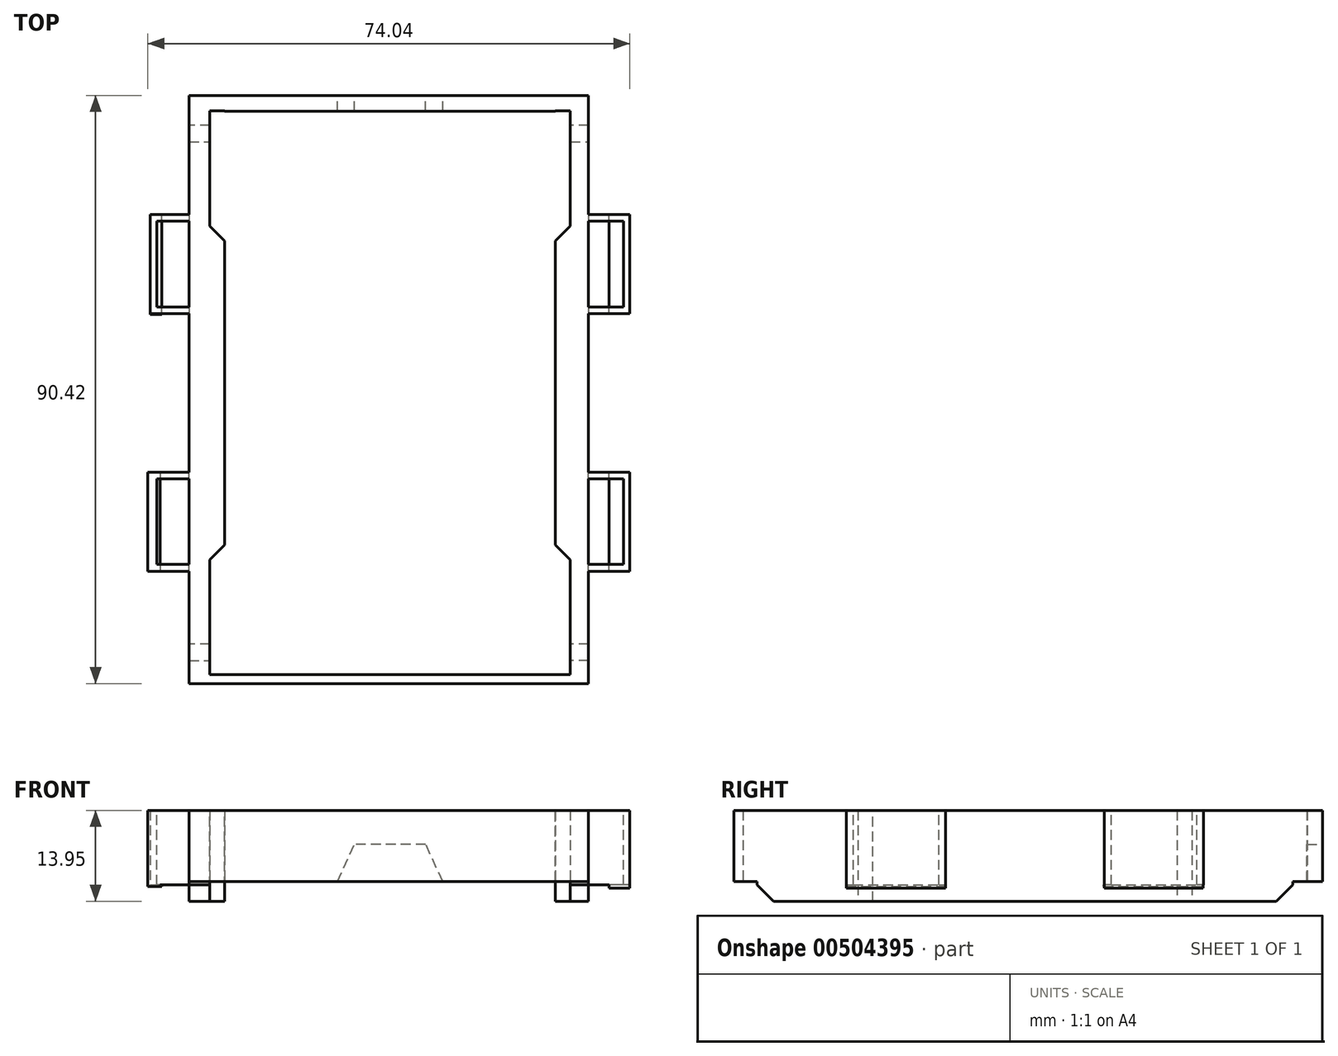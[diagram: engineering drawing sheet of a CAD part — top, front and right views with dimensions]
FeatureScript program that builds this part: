
annotation { "Feature Type Name" : "Feature", "Feature Type Description" : "" }
export const myFeature = defineFeature(function(context is Context, id is Id, definition is map)
    precondition{}
    {
        {
            var Q0;
            Q0=qCreatedBy(makeId("Top.planeOp"),FACE);
            var sketch = newSketch(context, id + "F0", { "sketchPlane" : qUnion([Q0])});
            skLineSegment(sketch, "E0.bottom", {"start": v(-30.48, 45.72) * mm, "end": v(30.48, 45.72) * mm});
            skLineSegment(sketch, "E0.top", {"start": v(-30.48, -45.72) * mm, "end": v(30.48, -45.72) * mm});
            skLineSegment(sketch, "E0.left", {"start": v(-30.48, 45.72) * mm, "end": v(-30.48, -45.72) * mm});
            skLineSegment(sketch, "E0.right", {"start": v(30.48, 45.72) * mm, "end": v(30.48, -45.72) * mm});
            skPoint(sketch, "E0.middle", {"position": v(0, 0) * mm});
            skLineSegment(sketch, "E1.bottom", {"start": v(-25.4, 43.3) * mm, "end": v(25.4, 43.3) * mm});
            skLineSegment(sketch, "E1.top", {"start": v(-25.4, -43.3) * mm, "end": v(25.4, -43.3) * mm});
            skLineSegment(sketch, "E1.left", {"start": v(-25.4, 43.3) * mm, "end": v(-25.4, -43.3) * mm});
            skLineSegment(sketch, "E1.right", {"start": v(25.4, 43.3) * mm, "end": v(25.4, -43.3) * mm});
            skSolve(sketch);
        }
        {
            var Q0;
            Q0=makeQuery(id+"F0.imprint","IMPRINT",FACE,{"disambiguationData":[TD([[makeQuery(id+"F0.imprint","IMPRINT",EDGE,{"derivedFrom":sQuery(id+"F0.wireOp",EDGE,"E0.bottom")}),-1.0]])]});
            extrude(context, id + "F1", {"entities" : qUnion([Q0]), "depth" : 28.45 * mm});
        }
        {
            var Q0;
            Q0=makeQuery(id+"F1.opExtrude","SWEPT_FACE",FACE,{"disambiguationData":[OSD([sQuery(id+"F0.wireOp",EDGE,"E0.bottom")])]});
            var sketch = newSketch(context, id + "F2", { "sketchPlane" : qUnion([Q0])});
            skLineSegment(sketch, "E2", {"start": v(30.48, 14.22) * mm, "end": v(-30.48, 14.22) * mm, "construction": true});
            skPoint(sketch, "E3.middle", {"position": v(0, 28.45) * mm});
            skLineSegment(sketch, "E4", {"start": v(0, 0) * mm, "end": v(-9.48, 0) * mm});
            skLineSegment(sketch, "E5.bottom", {"start": v(-5.46, 19.69) * mm, "end": v(5.46, 19.69) * mm});
            skLineSegment(sketch, "E5.top", {"start": v(-5.46, 8.76) * mm, "end": v(5.46, 8.76) * mm});
            skPoint(sketch, "E5.middle", {"position": v(0, 14.22) * mm});
            skLineSegment(sketch, "E6", {"start": v(-9.48, 0) * mm, "end": v(-5.46, 8.76) * mm});
            skLineSegment(sketch, "E7.MirrorCS", {"start": v(0, 0) * mm, "end": v(9.48, 0) * mm});
            skLineSegment(sketch, "E8.MirrorCS", {"start": v(9.48, 0) * mm, "end": v(5.46, 8.76) * mm});
            skLineSegment(sketch, "E9.MirrorCS", {"start": v(-5.46, 19.68) * mm, "end": v(5.46, 19.68) * mm});
            skLineSegment(sketch, "E10.MirrorCS", {"start": v(-9.48, 28.45) * mm, "end": v(-5.46, 19.68) * mm});
            skLineSegment(sketch, "E11.MirrorCS", {"start": v(0, 28.45) * mm, "end": v(-9.48, 28.45) * mm});
            skLineSegment(sketch, "E12.MirrorCS", {"start": v(0, 28.45) * mm, "end": v(9.48, 28.45) * mm});
            skLineSegment(sketch, "E13.MirrorCS", {"start": v(9.48, 28.45) * mm, "end": v(5.46, 19.68) * mm});
            skSolve(sketch);
        }
        {
            var Q0;
            Q0=qSketchRegion(id+"F2",true);
            var Q1;
            {var subQ1=sQuery(id+"F2.wireOp",EDGE,"z2dX2tQm-mAHQ-A0xj-hADe-n06FKAJlfdiZ.bottom");Q1=makeQuery(id+"F2.imprint","IMPRINT",FACE,{"disambiguationData":[TD([[makeQuery(id+"F2.imprint","IMPRINT",EDGE,{"derivedFrom":subQ1}),-1.0]])]});}
            extrude(context, id + "F3", {"entities" : qUnion([Q0, Q1]), "operationType" : NewBodyOperationType.REMOVE, "oppositeDirection" : true, "depth" : 25.4 * mm});
        }
        {
            var Q0;
            Q0=qCreatedBy(makeId("Top.planeOp"),FACE);
            var sketch = newSketch(context, id + "F4", { "sketchPlane" : qUnion([Q0])});
            skLineSegment(sketch, "E14.bottom", {"start": v(33.22, 48.14) * mm, "end": v(-33.43, 48.14) * mm});
            skLineSegment(sketch, "E14.top", {"start": v(33.22, 41.15) * mm, "end": v(-33.43, 41.15) * mm});
            skLineSegment(sketch, "E14.left", {"start": v(33.22, 48.14) * mm, "end": v(33.22, 41.15) * mm});
            skLineSegment(sketch, "E14.right", {"start": v(-33.43, 48.14) * mm, "end": v(-33.43, 41.15) * mm});
            skLineSegment(sketch, "E15.MirrorCS", {"start": v(33.22, -41.15) * mm, "end": v(-33.43, -41.15) * mm});
            skLineSegment(sketch, "E16.MirrorCS", {"start": v(33.22, -48.14) * mm, "end": v(33.22, -41.15) * mm});
            skLineSegment(sketch, "E17.MirrorCS", {"start": v(-33.43, -48.14) * mm, "end": v(-33.43, -41.15) * mm});
            skLineSegment(sketch, "E18.MirrorCS", {"start": v(33.22, -48.14) * mm, "end": v(-33.43, -48.14) * mm});
            skSolve(sketch);
        }
        {
            var Q0;
            Q0=qSketchRegion(id+"F4",true);
            extrude(context, id + "F5", {"entities" : qUnion([Q0]), "operationType" : NewBodyOperationType.REMOVE, "depth" : 3.05 * mm});
        }
        {
            var Q0;
            Q0=makeQuery(id+"F1.opExtrude","CAP_FACE",FACE,{"disambiguationData":[OSD([sQuery(id+"F0.wireOp",EDGE,"E0.bottom"),sQuery(id+"F0.wireOp",EDGE,"E0.top"),sQuery(id+"F0.wireOp",EDGE,"E0.left"),sQuery(id+"F0.wireOp",EDGE,"E0.right"),sQuery(id+"F0.wireOp",EDGE,"E1.bottom"),sQuery(id+"F0.wireOp",EDGE,"E1.top"),sQuery(id+"F0.wireOp",EDGE,"E1.left"),sQuery(id+"F0.wireOp",EDGE,"E1.right")])],"isStart":false});
            var sketch = newSketch(context, id + "F6", { "sketchPlane" : qUnion([Q0])});
            skLineSegment(sketch, "E19.bottom", {"start": v(30.48, 45.72) * mm, "end": v(-34.49, 45.72) * mm});
            skLineSegment(sketch, "E19.top", {"start": v(30.48, 40.94) * mm, "end": v(-34.49, 40.94) * mm});
            skLineSegment(sketch, "E19.left", {"start": v(30.48, 45.72) * mm, "end": v(30.48, 40.94) * mm});
            skLineSegment(sketch, "E19.right", {"start": v(-34.49, 45.72) * mm, "end": v(-34.49, 40.94) * mm});
            skLineSegment(sketch, "E20.MirrorCS", {"start": v(30.48, -40.94) * mm, "end": v(-34.49, -40.94) * mm});
            skLineSegment(sketch, "E21.MirrorCS", {"start": v(30.48, -45.72) * mm, "end": v(30.48, -40.94) * mm});
            skLineSegment(sketch, "E22.MirrorCS", {"start": v(-34.49, -45.72) * mm, "end": v(-34.49, -40.94) * mm});
            skLineSegment(sketch, "E23.MirrorCS", {"start": v(30.48, -45.72) * mm, "end": v(-34.49, -45.72) * mm});
            skSolve(sketch);
        }
        {
            var Q0;
            Q0=qSketchRegion(id+"F6",true);
            extrude(context, id + "F7", {"entities" : qUnion([Q0]), "operationType" : NewBodyOperationType.REMOVE, "oppositeDirection" : true, "depth" : 3.05 * mm});
        }
        {
            var Q0;
            Q0=makeQuery(id+"F1.opExtrude","SWEPT_FACE",FACE,{"disambiguationData":[OSD([sQuery(id+"F0.wireOp",EDGE,"E1.right")])]});
            var sketch = newSketch(context, id + "F8", { "sketchPlane" : qUnion([Q0])});
            skLineSegment(sketch, "E24.bottom", {"start": v(-41.15, 0) * mm, "end": v(-25.91, 0) * mm});
            skLineSegment(sketch, "E24.top", {"start": v(-41.15, 30.48) * mm, "end": v(-25.91, 30.48) * mm});
            skLineSegment(sketch, "E24.right", {"start": v(-25.91, 0) * mm, "end": v(-25.91, 30.48) * mm});
            skLineSegment(sketch, "E25", {"start": v(0, 0) * mm, "end": v(0, 28.45) * mm, "construction": true});
            skLineSegment(sketch, "E26.MirrorCS", {"start": v(25.91, 0) * mm, "end": v(25.91, 30.48) * mm});
            skLineSegment(sketch, "E27.MirrorCS", {"start": v(41.15, 30.48) * mm, "end": v(25.91, 30.48) * mm});
            skLineSegment(sketch, "E28.MirrorCS", {"start": v(41.15, 0) * mm, "end": v(25.91, 0) * mm});
            skLineSegment(sketch, "E29", {"start": v(-41.15, 30.48) * mm, "end": v(-43.09, 30.48) * mm});
            skLineSegment(sketch, "E30", {"start": v(-43.09, 30.48) * mm, "end": v(-43.09, 0) * mm});
            skLineSegment(sketch, "E31", {"start": v(-43.09, 0) * mm, "end": v(-41.15, 0) * mm});
            skLineSegment(sketch, "E32.MirrorCS", {"start": v(41.15, 30.48) * mm, "end": v(43.09, 30.48) * mm});
            skLineSegment(sketch, "E33.MirrorCS", {"start": v(43.09, 30.48) * mm, "end": v(43.09, 0) * mm});
            skLineSegment(sketch, "E34.MirrorCS", {"start": v(43.09, 0) * mm, "end": v(41.15, 0) * mm});
            skSolve(sketch);
        }
        {
            var Q0;
            Q0=qSketchRegion(id+"F8",true);
            extrude(context, id + "F9", {"entities" : qUnion([Q0]), "operationType" : NewBodyOperationType.REMOVE, "oppositeDirection" : true, "depth" : 2.3 * mm});
        }
        {
            var Q0;
            Q0=qCreatedBy(makeId("Right.planeOp"),FACE);
            var sketch = newSketch(context, id + "F10", { "sketchPlane" : qUnion([Q0])});
            skLineSegment(sketch, "E35.bottom", {"start": v(51.68, -10.67) * mm, "end": v(-48.17, -10.67) * mm});
            skLineSegment(sketch, "E35.top", {"start": v(51.68, 37.54) * mm, "end": v(-48.17, 37.54) * mm});
            skLineSegment(sketch, "E35.left", {"start": v(51.68, -10.67) * mm, "end": v(51.68, 37.54) * mm});
            skLineSegment(sketch, "E35.right", {"start": v(-48.17, -10.67) * mm, "end": v(-48.17, 37.54) * mm});
            skSolve(sketch);
        }
        {
            var Q0;
            Q0=qSketchRegion(id+"F10",true);
            extrude(context, id + "F11", {"entities" : qUnion([Q0]), "operationType" : NewBodyOperationType.REMOVE, "oppositeDirection" : true, "depth" : 50.8 * mm});
        }
        {
            var Q0;
            Q0=makeQuery(id+"F1.opExtrude","SWEPT_BODY",BODY,{"disambiguationData":[OSD([sQuery(id+"F0.wireOp",EDGE,"E0.bottom"),sQuery(id+"F0.wireOp",EDGE,"E0.top"),sQuery(id+"F0.wireOp",EDGE,"E0.left"),sQuery(id+"F0.wireOp",EDGE,"E0.right"),sQuery(id+"F0.wireOp",EDGE,"E1.bottom"),sQuery(id+"F0.wireOp",EDGE,"E1.top"),sQuery(id+"F0.wireOp",EDGE,"E1.left"),sQuery(id+"F0.wireOp",EDGE,"E1.right")])]});
            var Q1;
            Q1=qCreatedBy(makeId("Right.planeOp"),FACE);
            mirror(context, id + "F12", {"operationType" : NewBodyOperationType.ADD, "entities" : qUnion([Q0]), "mirrorPlane" : qUnion([Q1])});
        }
        {
            var Q0;
            {var subQ1=sQuery(id+"F0.wireOp",EDGE,"E0.right");var subQ2=sQuery(id+"F6.wireOp",EDGE,"E19.top");Q0=makeQuery(id+"F12.opPattern","COPY",EDGE,{"derivedFrom":makeQuery(id+"F7.boolean.opBoolean","COPY",EDGE,{"disambiguationData":[TD([makeQuery(id+"F1.opExtrude","SWEPT_FACE",FACE,{"disambiguationData":[OSD([subQ1])]})])],"derivedFrom":makeQuery(id+"F7.opExtrude","CAP_EDGE",EDGE,{"disambiguationData":[OSD([subQ2])],"isStart":true})}),"instanceName":"1"});}
            var Q1;
            {var subQ1=sQuery(id+"F0.wireOp",EDGE,"E0.right");var subQ2=sQuery(id+"F4.wireOp",EDGE,"E14.top");Q1=makeQuery(id+"F12.opPattern","COPY",EDGE,{"derivedFrom":makeQuery(id+"F5.boolean.opBoolean","COPY",EDGE,{"disambiguationData":[TD([makeQuery(id+"F1.opExtrude","SWEPT_FACE",FACE,{"disambiguationData":[OSD([subQ1])]})])],"derivedFrom":makeQuery(id+"F5.opExtrude","CAP_EDGE",EDGE,{"disambiguationData":[OSD([subQ2])],"isStart":true})}),"instanceName":"1"});}
            var Q2;
            {var subQ1=sQuery(id+"F0.wireOp",EDGE,"E0.right");var subQ2=sQuery(id+"F6.wireOp",EDGE,"E19.top");Q2=makeQuery(id+"F7.boolean.opBoolean","COPY",EDGE,{"disambiguationData":[TD([makeQuery(id+"F1.opExtrude","SWEPT_FACE",FACE,{"disambiguationData":[OSD([subQ1])]})])],"derivedFrom":makeQuery(id+"F7.opExtrude","CAP_EDGE",EDGE,{"disambiguationData":[OSD([subQ2])],"isStart":true})});}
            var Q3;
            {var subQ1=sQuery(id+"F0.wireOp",EDGE,"E0.right");var subQ2=sQuery(id+"F6.wireOp",EDGE,"E20.MirrorCS");Q3=makeQuery(id+"F7.boolean.opBoolean","COPY",EDGE,{"disambiguationData":[TD([makeQuery(id+"F1.opExtrude","SWEPT_FACE",FACE,{"disambiguationData":[OSD([subQ1])]})])],"derivedFrom":makeQuery(id+"F7.opExtrude","CAP_EDGE",EDGE,{"disambiguationData":[OSD([subQ2])],"isStart":true})});}
            var Q4;
            {var subQ1=sQuery(id+"F0.wireOp",EDGE,"E0.right");var subQ2=sQuery(id+"F6.wireOp",EDGE,"E20.MirrorCS");Q4=makeQuery(id+"F12.opPattern","COPY",EDGE,{"derivedFrom":makeQuery(id+"F7.boolean.opBoolean","COPY",EDGE,{"disambiguationData":[TD([makeQuery(id+"F1.opExtrude","SWEPT_FACE",FACE,{"disambiguationData":[OSD([subQ1])]})])],"derivedFrom":makeQuery(id+"F7.opExtrude","CAP_EDGE",EDGE,{"disambiguationData":[OSD([subQ2])],"isStart":true})}),"instanceName":"1"});}
            var Q5;
            {var subQ1=sQuery(id+"F0.wireOp",EDGE,"E0.right");var subQ2=sQuery(id+"F4.wireOp",EDGE,"E15.MirrorCS");Q5=makeQuery(id+"F12.opPattern","COPY",EDGE,{"derivedFrom":makeQuery(id+"F5.boolean.opBoolean","COPY",EDGE,{"disambiguationData":[TD([makeQuery(id+"F1.opExtrude","SWEPT_FACE",FACE,{"disambiguationData":[OSD([subQ1])]})])],"derivedFrom":makeQuery(id+"F5.opExtrude","CAP_EDGE",EDGE,{"disambiguationData":[OSD([subQ2])],"isStart":true})}),"instanceName":"1"});}
            var Q6;
            {var subQ1=sQuery(id+"F0.wireOp",EDGE,"E0.right");var subQ2=sQuery(id+"F4.wireOp",EDGE,"E15.MirrorCS");Q6=makeQuery(id+"F5.boolean.opBoolean","COPY",EDGE,{"disambiguationData":[TD([makeQuery(id+"F1.opExtrude","SWEPT_FACE",FACE,{"disambiguationData":[OSD([subQ1])]})])],"derivedFrom":makeQuery(id+"F5.opExtrude","CAP_EDGE",EDGE,{"disambiguationData":[OSD([subQ2])],"isStart":true})});}
            var Q7;
            {var subQ1=sQuery(id+"F0.wireOp",EDGE,"E0.right");var subQ2=sQuery(id+"F4.wireOp",EDGE,"E14.top");Q7=makeQuery(id+"F5.boolean.opBoolean","COPY",EDGE,{"disambiguationData":[TD([makeQuery(id+"F1.opExtrude","SWEPT_FACE",FACE,{"disambiguationData":[OSD([subQ1])]})])],"derivedFrom":makeQuery(id+"F5.opExtrude","CAP_EDGE",EDGE,{"disambiguationData":[OSD([subQ2])],"isStart":true})});}
            var Q8;
            Q8=makeQuery(id+"F9.boolean.opBoolean","COPY",EDGE,{"derivedFrom":makeQuery(id+"F9.opExtrude","CAP_EDGE",EDGE,{"disambiguationData":[OSD([sQuery(id+"F8.wireOp",EDGE,"E24.right")])],"isStart":true})});
            var Q9;
            Q9=makeQuery(id+"F9.boolean.opBoolean","COPY",EDGE,{"derivedFrom":makeQuery(id+"F9.opExtrude","CAP_EDGE",EDGE,{"disambiguationData":[OSD([sQuery(id+"F8.wireOp",EDGE,"E26.MirrorCS")])],"isStart":true})});
            var Q10;
            Q10=makeQuery(id+"F12.opPattern","COPY",EDGE,{"derivedFrom":makeQuery(id+"F9.boolean.opBoolean","COPY",EDGE,{"derivedFrom":makeQuery(id+"F9.opExtrude","CAP_EDGE",EDGE,{"disambiguationData":[OSD([sQuery(id+"F8.wireOp",EDGE,"E24.right")])],"isStart":true})}),"instanceName":"1"});
            var Q11;
            Q11=makeQuery(id+"F12.opPattern","COPY",EDGE,{"derivedFrom":makeQuery(id+"F9.boolean.opBoolean","COPY",EDGE,{"derivedFrom":makeQuery(id+"F9.opExtrude","CAP_EDGE",EDGE,{"disambiguationData":[OSD([sQuery(id+"F8.wireOp",EDGE,"E26.MirrorCS")])],"isStart":true})}),"instanceName":"1"});
            chamfer(context, id + "F13", {"entities" : qUnion([Q0, Q1, Q2, Q3, Q4, Q5, Q6, Q7, Q8, Q9, Q10, Q11]), "width" : 2.54 * mm, "tangentPropagation" : true});
        }
        {
            var Q0;
            Q0=makeQuery(id+"F1.opExtrude","SWEPT_FACE",FACE,{"disambiguationData":[OSD([sQuery(id+"F0.wireOp",EDGE,"E0.right")])]});
            var sketch = newSketch(context, id + "F14", { "sketchPlane" : qUnion([Q0])});
            skLineSegment(sketch, "E36.bottom", {"start": v(-27.43, 25.9) * mm, "end": v(-12.2, 25.9) * mm});
            skLineSegment(sketch, "E36.top", {"start": v(-27.43, 2.54) * mm, "end": v(-12.2, 2.54) * mm});
            skLineSegment(sketch, "E36.left", {"start": v(-27.43, 25.9) * mm, "end": v(-27.43, 2.54) * mm});
            skLineSegment(sketch, "E36.right", {"start": v(-12.2, 25.9) * mm, "end": v(-12.2, 2.54) * mm});
            skLineSegment(sketch, "E37.MirrorCS", {"start": v(12.2, 25.9) * mm, "end": v(12.2, 2.54) * mm});
            skLineSegment(sketch, "E38.MirrorCS", {"start": v(27.43, 25.9) * mm, "end": v(12.2, 25.9) * mm});
            skLineSegment(sketch, "E39.MirrorCS", {"start": v(27.43, 2.54) * mm, "end": v(12.2, 2.54) * mm});
            skLineSegment(sketch, "E40.MirrorCS", {"start": v(27.43, 25.9) * mm, "end": v(27.43, 2.54) * mm});
            skSolve(sketch);
        }
        {
            var Q0;
            Q0=qSketchRegion(id+"F14",true);
            extrude(context, id + "F15", {"entities" : qUnion([Q0]), "operationType" : NewBodyOperationType.ADD, "depth" : 6.35 * mm});
        }
        {
            var Q0;
            Q0=makeQuery(id+"F15.opExtrude","SWEPT_FACE",FACE,{"disambiguationData":[OSD([sQuery(id+"F14.wireOp",EDGE,"E36.bottom")])]});
            var sketch = newSketch(context, id + "F16", { "sketchPlane" : qUnion([Q0])});
            skLineSegment(sketch, "E41.bottom", {"start": v(30.48, -26.38) * mm, "end": v(35.84, -26.38) * mm});
            skLineSegment(sketch, "E41.top", {"start": v(30.48, -13.23) * mm, "end": v(35.84, -13.23) * mm});
            skLineSegment(sketch, "E41.left", {"start": v(30.48, -26.38) * mm, "end": v(30.48, -13.23) * mm});
            skLineSegment(sketch, "E41.right", {"start": v(35.84, -26.38) * mm, "end": v(35.84, -13.23) * mm});
            skLineSegment(sketch, "E42.MirrorCS", {"start": v(30.48, 13.23) * mm, "end": v(35.84, 13.23) * mm});
            skLineSegment(sketch, "E43.MirrorCS", {"start": v(35.84, 26.38) * mm, "end": v(35.84, 13.23) * mm});
            skLineSegment(sketch, "E44.MirrorCS", {"start": v(30.48, 26.38) * mm, "end": v(35.84, 26.38) * mm});
            skLineSegment(sketch, "E45.MirrorCS", {"start": v(30.48, 26.38) * mm, "end": v(30.48, 13.23) * mm});
            skSolve(sketch);
        }
        {
            var Q0;
            Q0=qSketchRegion(id+"F16",true);
            extrude(context, id + "F17", {"entities" : qUnion([Q0]), "operationType" : NewBodyOperationType.REMOVE, "endBound" : BoundingType.THROUGH_ALL, "oppositeDirection" : true, "depth" : 25.4 * mm});
        }
        {
            var Q0;
            Q0=makeQuery(id+"F1.opExtrude","SWEPT_BODY",BODY,{"disambiguationData":[OSD([sQuery(id+"F0.wireOp",EDGE,"E0.bottom"),sQuery(id+"F0.wireOp",EDGE,"E0.top"),sQuery(id+"F0.wireOp",EDGE,"E0.left"),sQuery(id+"F0.wireOp",EDGE,"E0.right"),sQuery(id+"F0.wireOp",EDGE,"E1.bottom"),sQuery(id+"F0.wireOp",EDGE,"E1.top"),sQuery(id+"F0.wireOp",EDGE,"E1.left"),sQuery(id+"F0.wireOp",EDGE,"E1.right")])]});
            var Q1;
            Q1=qCreatedBy(makeId("Right.planeOp"),FACE);
            mirror(context, id + "F18", {"operationType" : NewBodyOperationType.ADD, "entities" : qUnion([Q0]), "mirrorPlane" : qUnion([Q1])});
        }
        {
            var Q0;
            Q0=makeQuery(id+"F9.boolean.opBoolean","COPY",FACE,{"derivedFrom":makeQuery(id+"F9.opExtrude","SWEPT_FACE",FACE,{"disambiguationData":[OSD([sQuery(id+"F8.wireOp",EDGE,"E33.MirrorCS")])]})});
            var Q1;
            Q1=makeQuery(id+"F12.opPattern","COPY",FACE,{"derivedFrom":makeQuery(id+"F9.boolean.opBoolean","COPY",FACE,{"derivedFrom":makeQuery(id+"F9.opExtrude","SWEPT_FACE",FACE,{"disambiguationData":[OSD([sQuery(id+"F8.wireOp",EDGE,"E33.MirrorCS")])]})}),"instanceName":"1"});
            extrude(context, id + "F19", {"entities" : qUnion([Q0, Q1]), "operationType" : NewBodyOperationType.REMOVE, "oppositeDirection" : true, "depth" : 0.25 * mm});
        }
        {
            var Q0;
            Q0=makeQuery(id+"F9.boolean.opBoolean","COPY",FACE,{"derivedFrom":makeQuery(id+"F9.opExtrude","SWEPT_FACE",FACE,{"disambiguationData":[OSD([sQuery(id+"F8.wireOp",EDGE,"E30")])]})});
            var Q1;
            Q1=makeQuery(id+"F12.opPattern","COPY",FACE,{"derivedFrom":makeQuery(id+"F9.boolean.opBoolean","COPY",FACE,{"derivedFrom":makeQuery(id+"F9.opExtrude","SWEPT_FACE",FACE,{"disambiguationData":[OSD([sQuery(id+"F8.wireOp",EDGE,"E30")])]})}),"instanceName":"1"});
            extrude(context, id + "F20", {"entities" : qUnion([Q0, Q1]), "operationType" : NewBodyOperationType.REMOVE, "oppositeDirection" : true, "depth" : 0.25 * mm});
        }
        {
            var Q0;
            {var subQ0=makeQuery(id+"F1.opExtrude","SWEPT_FACE",FACE,{"disambiguationData":[OSD([sQuery(id+"F0.wireOp",EDGE,"E0.top")])]});Q0=makeQuery(id+"F12.boolean.opBoolean","MERGE",FACE,{"derivedFrom":[subQ0,makeQuery(id+"F12.opPattern","COPY",FACE,{"derivedFrom":subQ0,"instanceName":"1"})]});}
            extrude(context, id + "F21", {"entities" : qUnion([Q0]), "operationType" : NewBodyOperationType.REMOVE, "oppositeDirection" : true, "depth" : 1.02 * mm});
        }
        {
            var Q0;
            Q0=makeQuery(id+"F18.opPattern","COPY",FACE,{"derivedFrom":makeQuery(id+"F15.opExtrude","SWEPT_FACE",FACE,{"disambiguationData":[OSD([sQuery(id+"F14.wireOp",EDGE,"E38.MirrorCS")])]}),"instanceName":"1"});
            var sketch = newSketch(context, id + "F22", { "sketchPlane" : qUnion([Q0])});
            skLineSegment(sketch, "E46.bottom", {"start": v(-36.83, 27.43) * mm, "end": v(-33.66, 27.43) * mm});
            skLineSegment(sketch, "E46.top", {"start": v(-36.83, 12.2) * mm, "end": v(-33.66, 12.2) * mm});
            skLineSegment(sketch, "E46.left", {"start": v(-36.83, 27.43) * mm, "end": v(-36.83, 12.2) * mm});
            skLineSegment(sketch, "E46.right", {"start": v(-33.66, 27.43) * mm, "end": v(-33.66, 12.2) * mm});
            skLineSegment(sketch, "E47.bottom", {"start": v(-33.66, -12.01) * mm, "end": v(-36.83, -12.01) * mm});
            skLineSegment(sketch, "E47.top", {"start": v(-33.66, -27.44) * mm, "end": v(-36.83, -27.44) * mm});
            skLineSegment(sketch, "E47.left", {"start": v(-33.66, -12.01) * mm, "end": v(-33.66, -27.44) * mm});
            skLineSegment(sketch, "E47.right", {"start": v(-36.83, -12.01) * mm, "end": v(-36.83, -27.44) * mm});
            skSolve(sketch);
        }
        {
            var Q0;
            Q0=qSketchRegion(id+"F22",true);
            extrude(context, id + "F23", {"entities" : qUnion([Q0]), "operationType" : NewBodyOperationType.ADD, "depth" : 0.5 * mm});
        }
        {
            var Q0;
            Q0=makeQuery(id+"F15.opExtrude","SWEPT_FACE",FACE,{"disambiguationData":[OSD([sQuery(id+"F14.wireOp",EDGE,"E36.top")])]});
            var sketch = newSketch(context, id + "F24", { "sketchPlane" : qUnion([Q0])});
            skLineSegment(sketch, "E48.bottom", {"start": v(36.83, 27.43) * mm, "end": v(33.66, 27.43) * mm});
            skLineSegment(sketch, "E48.top", {"start": v(36.83, 12.2) * mm, "end": v(33.66, 12.2) * mm});
            skLineSegment(sketch, "E48.left", {"start": v(36.83, 27.43) * mm, "end": v(36.83, 12.2) * mm});
            skLineSegment(sketch, "E48.right", {"start": v(33.66, 27.43) * mm, "end": v(33.66, 12.2) * mm});
            skLineSegment(sketch, "E49.bottom", {"start": v(36.83, -12.2) * mm, "end": v(33.66, -12.2) * mm});
            skLineSegment(sketch, "E49.top", {"start": v(36.83, -27.38) * mm, "end": v(33.66, -27.38) * mm});
            skLineSegment(sketch, "E49.left", {"start": v(36.83, -12.2) * mm, "end": v(36.83, -27.38) * mm});
            skLineSegment(sketch, "E49.right", {"start": v(33.66, -12.2) * mm, "end": v(33.66, -27.38) * mm});
            skSolve(sketch);
        }
        {
            var Q0;
            Q0=qSketchRegion(id+"F24",true);
            extrude(context, id + "F25", {"entities" : qUnion([Q0]), "operationType" : NewBodyOperationType.ADD, "depth" : 0.5 * mm});
        }
        {
            var Q0;
            Q0=makeQuery(id+"F15.opExtrude","SWEPT_FACE",FACE,{"disambiguationData":[OSD([sQuery(id+"F14.wireOp",EDGE,"E36.bottom")])]});
            var sketch = newSketch(context, id + "F26", { "sketchPlane" : qUnion([Q0])});
            skLineSegment(sketch, "E50.bottom", {"start": v(36.83, -27.43) * mm, "end": v(35.34, -27.43) * mm});
            skLineSegment(sketch, "E50.top", {"start": v(36.83, -12.2) * mm, "end": v(35.34, -12.2) * mm});
            skLineSegment(sketch, "E50.left", {"start": v(36.83, -27.43) * mm, "end": v(36.83, -12.2) * mm});
            skLineSegment(sketch, "E50.right", {"start": v(35.34, -27.43) * mm, "end": v(35.34, -12.2) * mm});
            skLineSegment(sketch, "E51.bottom", {"start": v(35.34, 12.22) * mm, "end": v(36.83, 12.22) * mm});
            skLineSegment(sketch, "E51.top", {"start": v(35.34, 27.38) * mm, "end": v(36.83, 27.38) * mm});
            skLineSegment(sketch, "E51.left", {"start": v(35.34, 12.22) * mm, "end": v(35.34, 27.38) * mm});
            skLineSegment(sketch, "E51.right", {"start": v(36.83, 12.22) * mm, "end": v(36.83, 27.38) * mm});
            skSolve(sketch);
        }
        {
            var Q0;
            Q0=qSketchRegion(id+"F26",true);
            extrude(context, id + "F27", {"entities" : qUnion([Q0]), "operationType" : NewBodyOperationType.ADD, "depth" : 0.5 * mm});
        }
        {
            var Q0;
            Q0=makeQuery(id+"F18.opPattern","COPY",FACE,{"derivedFrom":makeQuery(id+"F15.opExtrude","SWEPT_FACE",FACE,{"disambiguationData":[OSD([sQuery(id+"F14.wireOp",EDGE,"E36.top")])]}),"instanceName":"1"});
            var sketch = newSketch(context, id + "F28", { "sketchPlane" : qUnion([Q0])});
            skLineSegment(sketch, "E52.bottom", {"start": v(-36.83, 12.2) * mm, "end": v(-35.32, 12.2) * mm});
            skLineSegment(sketch, "E52.top", {"start": v(-36.83, 27.43) * mm, "end": v(-35.32, 27.43) * mm});
            skLineSegment(sketch, "E52.left", {"start": v(-36.83, 12.2) * mm, "end": v(-36.83, 27.43) * mm});
            skLineSegment(sketch, "E52.right", {"start": v(-35.32, 12.2) * mm, "end": v(-35.32, 27.43) * mm});
            skLineSegment(sketch, "E53.bottom", {"start": v(-36.83, -12.06) * mm, "end": v(-35.34, -12.06) * mm});
            skLineSegment(sketch, "E53.top", {"start": v(-36.83, -27.45) * mm, "end": v(-35.34, -27.45) * mm});
            skLineSegment(sketch, "E53.left", {"start": v(-36.83, -12.06) * mm, "end": v(-36.83, -27.45) * mm});
            skLineSegment(sketch, "E53.right", {"start": v(-35.34, -12.06) * mm, "end": v(-35.34, -27.45) * mm});
            skSolve(sketch);
        }
        {
            var Q0;
            Q0=qSketchRegion(id+"F28",true);
            extrude(context, id + "F29", {"entities" : qUnion([Q0]), "operationType" : NewBodyOperationType.ADD, "depth" : 0.25 * mm});
        }
        {
            var Q0;
            Q0=makeQuery(id+"F12.opPattern","COPY",FACE,{"derivedFrom":makeQuery(id+"F1.opExtrude","SWEPT_FACE",FACE,{"disambiguationData":[OSD([sQuery(id+"F0.wireOp",EDGE,"E0.right")])]}),"instanceName":"1"});
            var Q1;
            Q1=makeQuery(id+"F29.opExtrude","SWEPT_FACE",FACE,{"disambiguationData":[OSD([sQuery(id+"F28.wireOp",EDGE,"E52.right")])]});
            var Q2;
            Q2=makeQuery(id+"F18.opPattern","COPY",FACE,{"derivedFrom":makeQuery(id+"F17.boolean.opBoolean","COPY",FACE,{"derivedFrom":makeQuery(id+"F17.opExtrude","SWEPT_FACE",FACE,{"disambiguationData":[OSD([sQuery(id+"F16.wireOp",EDGE,"E41.right")])]})}),"instanceName":"1"});
            var Q3;
            Q3=makeQuery(id+"F29.boolean.opBoolean","MERGE",FACE,{"derivedFrom":[makeQuery(id+"F23.boolean.opBoolean","MERGE",FACE,{"derivedFrom":[makeQuery(id+"F18.opPattern","COPY",FACE,{"derivedFrom":makeQuery(id+"F15.opExtrude","CAP_FACE",FACE,{"disambiguationData":[OSD([sQuery(id+"F14.wireOp",EDGE,"E36.bottom"),sQuery(id+"F14.wireOp",EDGE,"E36.top"),sQuery(id+"F14.wireOp",EDGE,"E36.left"),sQuery(id+"F14.wireOp",EDGE,"E36.right")])],"isStart":false}),"instanceName":"1"}),makeQuery(id+"F23.opExtrude","SWEPT_FACE",FACE,{"disambiguationData":[OSD([sQuery(id+"F22.wireOp",EDGE,"E47.right")])]})]}),makeQuery(id+"F29.opExtrude","SWEPT_FACE",FACE,{"disambiguationData":[OSD([sQuery(id+"F28.wireOp",EDGE,"E52.left")])]})]});
            extrude(context, id + "F30", {"entities" : qUnion([Q0, Q1, Q2, Q3]), "operationType" : NewBodyOperationType.ADD, "depth" : 0.38 * mm});
        }
        {
            var Q0;
            Q0=makeQuery(id+"F29.opExtrude","SWEPT_FACE",FACE,{"disambiguationData":[OSD([sQuery(id+"F28.wireOp",EDGE,"E53.right")])]});
            extrude(context, id + "F31", {"entities" : qUnion([Q0]), "operationType" : NewBodyOperationType.ADD, "depth" : 0.25 * mm});
        }
        {
            var Q0;
            {var subQ0=sQuery(id+"F0.wireOp",EDGE,"E0.right");var subQ1=sQuery(id+"F0.wireOp",EDGE,"E1.right");Q0=makeQuery(id+"F7.boolean.opBoolean","SPLIT",FACE,{"disambiguationData":[TD([makeQuery(id+"F1.opExtrude","SWEPT_FACE",FACE,{"disambiguationData":[OSD([subQ0])]})])],"derivedFrom":makeQuery(id+"F1.opExtrude","CAP_FACE",FACE,{"disambiguationData":[OSD([sQuery(id+"F0.wireOp",EDGE,"E0.bottom"),sQuery(id+"F0.wireOp",EDGE,"E0.top"),sQuery(id+"F0.wireOp",EDGE,"E0.left"),subQ0,sQuery(id+"F0.wireOp",EDGE,"E1.bottom"),sQuery(id+"F0.wireOp",EDGE,"E1.top"),sQuery(id+"F0.wireOp",EDGE,"E1.left"),subQ1])],"isStart":false})});}
            var sketch = newSketch(context, id + "F32", { "sketchPlane" : qUnion([Q0])});
            skLineSegment(sketch, "E54.bottom", {"start": v(64.06, -66.08) * mm, "end": v(-41.9, -66.08) * mm});
            skLineSegment(sketch, "E54.top", {"start": v(64.06, 50.2) * mm, "end": v(-41.9, 50.2) * mm});
            skLineSegment(sketch, "E54.left", {"start": v(64.06, -66.08) * mm, "end": v(64.06, 50.2) * mm});
            skLineSegment(sketch, "E54.right", {"start": v(-41.9, -66.08) * mm, "end": v(-41.9, 50.2) * mm});
            skSolve(sketch);
        }
        {
            var Q0;
            Q0=qSketchRegion(id+"F32",true);
            extrude(context, id + "F33", {"entities" : qUnion([Q0]), "operationType" : NewBodyOperationType.REMOVE, "oppositeDirection" : true, "depth" : 14.5 * mm});
        }
    });
